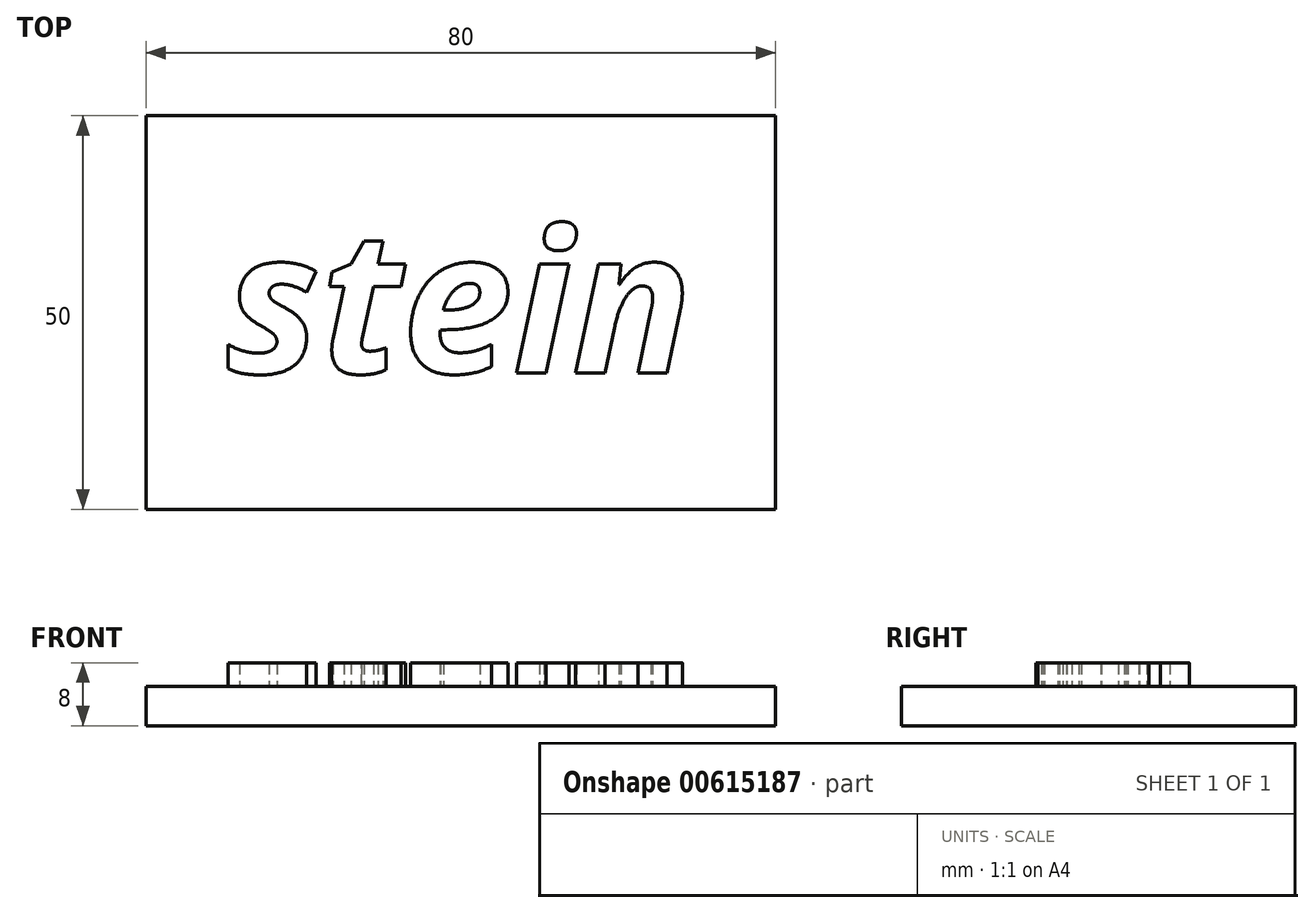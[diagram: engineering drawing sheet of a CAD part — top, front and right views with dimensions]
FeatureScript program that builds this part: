
annotation { "Feature Type Name" : "Feature", "Feature Type Description" : "" }
export const myFeature = defineFeature(function(context is Context, id is Id, definition is map)
    precondition{}
    {
        {
            var Q0;
            Q0=qCreatedBy(makeId("Top.planeOp"),FACE);
            var sketch = newSketch(context, id + "F0", { "sketchPlane" : qUnion([Q0])});
            skLineSegment(sketch, "E0.bottom", {"start": v(0, 0) * mm, "end": v(80, 0) * mm});
            skLineSegment(sketch, "E0.top", {"start": v(0, 50) * mm, "end": v(80, 50) * mm});
            skLineSegment(sketch, "E0.left", {"start": v(0, 0) * mm, "end": v(0, 50) * mm});
            skLineSegment(sketch, "E0.right", {"start": v(80, 0) * mm, "end": v(80, 50) * mm});
            skSolve(sketch);
        }
        {
            var Q0;
            Q0=makeQuery(id+"F0.imprint","IMPRINT",FACE,{"disambiguationData":[TD([[makeQuery(id+"F0.imprint","IMPRINT",EDGE,{"derivedFrom":sQuery(id+"F0.wireOp",EDGE,"E0.bottom")}),1.0]])]});
            extrude(context, id + "F1", {"entities" : qUnion([Q0]), "depth" : 5 * mm, "offsetDistance" : 25 * mm});
        }
        {
            var Q0;
            Q0=makeQuery(id+"F1.opExtrude","CAP_FACE",FACE,{"disambiguationData":[OSD([sQuery(id+"F0.wireOp",EDGE,"E0.bottom"),sQuery(id+"F0.wireOp",EDGE,"E0.top"),sQuery(id+"F0.wireOp",EDGE,"E0.left"),sQuery(id+"F0.wireOp",EDGE,"E0.right")])],"isStart":false});
            var sketch = newSketch(context, id + "F2", { "sketchPlane" : qUnion([Q0])});
            skText(sketch, "E1", { "text": "stein", "fontName": "OpenSans-BoldItalic.ttf"});
            const initialGuessF2  = {"E1": [0.01017, 0.01732, 1, 0, 0.01822]};
            skSetInitialGuess(sketch, initialGuessF2);
            skSolve(sketch);
        }
        {
            var Q0;
            Q0 = qSketchRegion(id + "F2", true);
            extrude(context, id + "F3", {"entities" : qUnion([Q0]), "operationType" : NewBodyOperationType.ADD, "depth" : 3 * mm, "offsetDistance" : 25 * mm});
        }
    });
